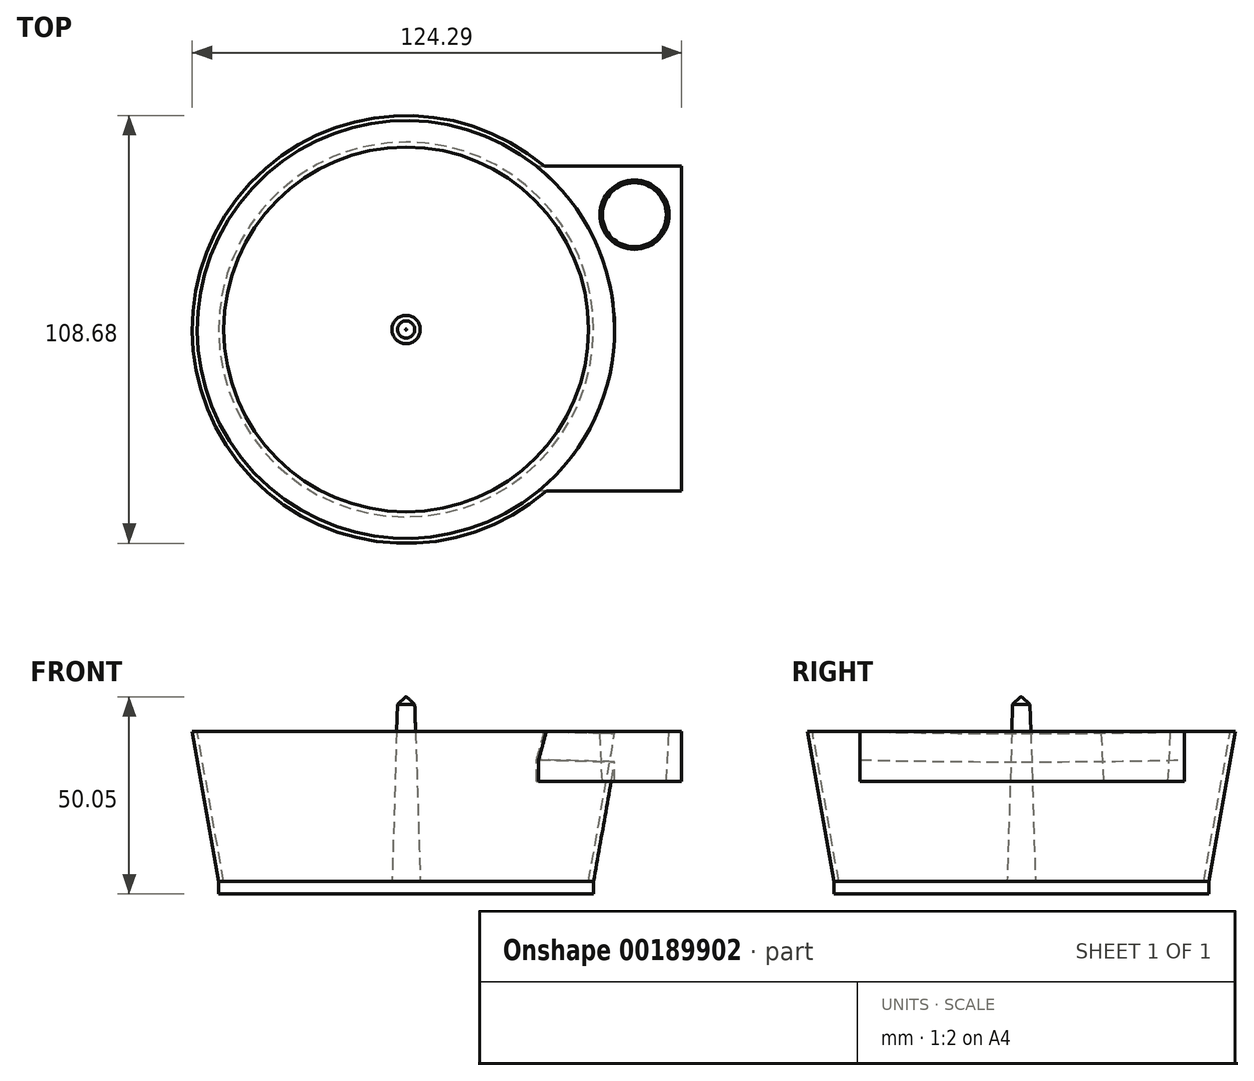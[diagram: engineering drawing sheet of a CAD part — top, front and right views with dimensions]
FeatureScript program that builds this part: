
annotation { "Feature Type Name" : "Feature", "Feature Type Description" : "" }
export const myFeature = defineFeature(function(context is Context, id is Id, definition is map)
    precondition{}
    {
        {
            var Q0;
            Q0=qCreatedBy(makeId("Top.planeOp"),FACE);
            var sketch = newSketch(context, id + "F0", { "sketchPlane" : qUnion([Q0])});
            skCircle(sketch, "E0", {"center": v(0, 0) * mm, "radius": 47.63 * mm});
            skSolve(sketch);
        }
        {
            var Q0;
            Q0=makeQuery(id+"F0.imprint","IMPRINT",FACE,{"disambiguationData":[TD([[makeQuery(id+"F0.imprint","IMPRINT",EDGE,{"derivedFrom":sQuery(id+"F0.wireOp",EDGE,"E0")}),1.0]])]});
            var Q1;
            Q1=sQuery(id+"F0.wireOp",EDGE,"E0");
            extrude(context, id + "F1", {"entities" : qUnion([Q0]), "surfaceEntities" : qUnion([Q1]), "depth" : 38.1 * mm, "hasDraft" : true, "draftAngle" : 10 * degree});
        }
        {
            var Q0;
            Q0=qCreatedBy(makeId("Top.planeOp"),FACE);
            var sketch = newSketch(context, id + "F2", { "sketchPlane" : qUnion([Q0])});
            skCircle(sketch, "E1", {"center": v(0, 0) * mm, "radius": 46.35 * mm});
            skSolve(sketch);
        }
        {
            var Q0;
            Q0 = qSketchRegion(id + "F2", true);
            extrude(context, id + "F3", {"entities" : qUnion([Q0]), "operationType" : NewBodyOperationType.REMOVE, "depth" : 38.1 * mm, "hasDraft" : true, "draftAngle" : 10 * degree});
        }
        {
            var Q0;
            Q0 = qSketchRegion(id + "F0", true);
            extrude(context, id + "F4", {"entities" : qUnion([Q0]), "operationType" : NewBodyOperationType.ADD, "oppositeDirection" : true, "depth" : 3.17 * mm});
        }
        {
            var Q0;
            Q0=qCreatedBy(makeId("Front.planeOp"),FACE);
            var sketch = newSketch(context, id + "F5", { "sketchPlane" : qUnion([Q0])});
            skLineSegment(sketch, "E2", {"start": v(0, 0) * mm, "end": v(0, 46.87) * mm});
            skLineSegment(sketch, "E3", {"start": v(0, 46.87) * mm, "end": v(2.13, 46.87) * mm});
            skLineSegment(sketch, "E4", {"start": v(2.13, 46.87) * mm, "end": v(3.6, 0) * mm});
            skLineSegment(sketch, "E5", {"start": v(3.6, 0) * mm, "end": v(0, 0) * mm});
            skSolve(sketch);
        }
        {
            var Q0;
            Q0=makeQuery(id+"F5.imprint","IMPRINT",FACE,{"disambiguationData":[TD([[makeQuery(id+"F5.imprint","IMPRINT",EDGE,{"derivedFrom":sQuery(id+"F5.wireOp",EDGE,"E2")}),-1.0]])]});
            var Q1;
            Q1=makeQuery(id+"F3.boolean.opBoolean","COPY",FACE,{"derivedFrom":makeQuery(id+"F3.opExtrude","SWEPT_FACE",FACE,{"disambiguationData":[OSD([sQuery(id+"F2.wireOp",EDGE,"E1")])]})});
            revolve(context, id + "F6", {"operationType" : NewBodyOperationType.ADD, "entities" : qUnion([Q0]), "axis" : qUnion([Q1]), "revolveType" : RevolveType.FULL});
        }
        {
            var Q0;
            Q0=makeQuery(id+"F6.opRevolve","SWEPT_EDGE",EDGE,{"disambiguationData":[OSD([sQuery(id+"F5.wireOp",EDGE,"E3"),sQuery(id+"F5.wireOp",EDGE,"E4")])]});
            chamfer(context, id + "F7", {"entities" : qUnion([Q0]), "width" : 2.03 * mm, "tangentPropagation" : true});
        }
        {
            var Q0;
            Q0=makeQuery(id+"F1.opExtrude","CAP_FACE",FACE,{"disambiguationData":[OSD([sQuery(id+"F0.wireOp",EDGE,"E0")])],"isStart":false});
            var sketch = newSketch(context, id + "F8", { "sketchPlane" : qUnion([Q0])});
            skLineSegment(sketch, "E6", {"start": v(33.12, 41.47) * mm, "end": v(69.95, 41.47) * mm});
            skLineSegment(sketch, "E7", {"start": v(69.95, 41.47) * mm, "end": v(69.95, -41.03) * mm});
            skLineSegment(sketch, "E8", {"start": v(69.95, -41.03) * mm, "end": v(33.67, -41.03) * mm});
            skArc(sketch, "E9", {"start": v(33.67, -41.03) * mm, "mid": v(52.98, 0.35) * mm, "end": v(33.12, 41.47) * mm});
            skSolve(sketch);
        }
        {
            var Q0;
            Q0 = qSketchRegion(id + "F8", true);
            extrude(context, id + "F9", {"entities" : qUnion([Q0]), "operationType" : NewBodyOperationType.ADD, "oppositeDirection" : true, "depth" : 12.7 * mm});
        }
        {
            var Q0;
            Q0=makeQuery(id+"F9.opExtrude","CAP_FACE",FACE,{"disambiguationData":[OSD([sQuery(id+"F8.wireOp",EDGE,"E6"),sQuery(id+"F8.wireOp",EDGE,"E7"),sQuery(id+"F8.wireOp",EDGE,"E8"),sQuery(id+"F8.wireOp",EDGE,"E9")])],"isStart":false});
            var sketch = newSketch(context, id + "F10", { "sketchPlane" : qUnion([Q0])});
            skCircle(sketch, "E10", {"center": v(58, -29.16) * mm, "radius": 8.13 * mm});
            skSolve(sketch);
        }
        {
            var Q0;
            Q0 = qSketchRegion(id + "F10", true);
            extrude(context, id + "F11", {"entities" : qUnion([Q0]), "operationType" : NewBodyOperationType.REMOVE, "oppositeDirection" : true, "depth" : 25.4 * mm, "hasDraft" : true, "draftAngle" : 3 * degree});
        }
    });
